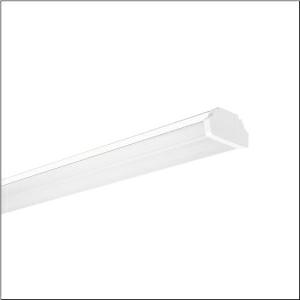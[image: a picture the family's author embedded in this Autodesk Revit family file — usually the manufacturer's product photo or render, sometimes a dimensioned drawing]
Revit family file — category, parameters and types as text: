
# Revit family: dus_31_gen_2_53bd812dv6a5c2_974b
name_source: partatom
category: Lighting Fixtures
units: mm (PartAtom-declared; Revit-internal decimal feet)

## family parameters
Cut with Voids When Loaded = No
Host = Face
Light Source = No
Part Type = Normal
Room Calculation Point = No
Round Connector Dimension = Use Diameter
Shared = No

## types (1)
- --- (1 x LED, 10550 lm, 61.4 W, 6500K)
    Apparent Load = 61 VA
    CIE Flux Codes = 47 80 95 93 100
    Color Rendering = 80
    Color Temperature = 6500K
    Default Elevation = 1800 mm
    Description = DUS 31 Gen.2, luminaire insert, of sheet steel, coil coated, white, length: 1.535mm, width: 81mm, height: 90mm, 5x system unit, system units: 307mm, LED rated luminous flux: 10.550lm, light colour: 865, SDCM (Standard Deviation of Colour Matching)MacAdam ≤ 3 SDCM (initial), control gear: DALI 2, control gear: ECG DALI, with plug, 5-pole, with phase selection, mains connection: 220..240V, AC, 50/60Hz, rated input power: 61W, through-wiring accessed according to module size, primary optical cover: cover, of PMMA, light emission: direct distribution, primary light characteristic: symmetric, protection rating (complete): IP20, protection rating (LED compartment): IP50, insulation class (complete): insulation class I (protective earthing), certification: CE, ENEC, VDE, UKCA, impact resistance: IK03, permissible ambient temperature for indoor applications: -25..+35°C, corresponds to IFS (International Featured Standards) requirements for safety and quality in the food industry, reducing of maximum allowable ambient temperature of 5°C with ceiling mounting, packaging unit: 1 piece
    Height = 95 mm
    Lamp = 1 x LED
    Lamp Light Flux = 10550 lm
    Lamp Power = 61.4 W
    Lamp count = 1
    Length = 1535 mm
    Luminous efficacy = 172 lm/W
    Manufacturer = Siteco
    ModVariant = No
    Model = 53BD812DV6A5C2
    Mounting Place = Ceiling
    Mounting Type = Pendant
    Number of Poles = 1
    OnlyDefault = Yes
    Power Factor = 1
    Product Name = DUS 31 Gen.2
    Product group = luminaire insert | ceiling pendant
    ProductGroupID = 901
    Protection Class = Protection class I
    Protection Degree = IP 20
    RLX_Detail_Level = 1
    RLX_Emergency_Light_Flux = 0 lm
    RLX_Emergency_Type = 0
    RLX_Emergency_Type_DB = No
    RlxData = <blob elided: 32113 chars, md5=6037fcd4>
    Socket = socket
    Standby Power = 0 W
    System Light Flux = 10550 lm
    System Power = 61 W
    Type Comments = factory setting: luminous flux: 100 % | dim-lin: 254 | 418 mA
    Type Image = l_1319596.jpg
    URL = http://relux.com
    VarID = @adj_001873
    Voltage = 0 V
    Weight = 0.00 kg
    Width = 81 mm

## geometry (parser evidence)
native form markers: Blend x4, Sweep x13
no freeform markers — native parametric forms only
